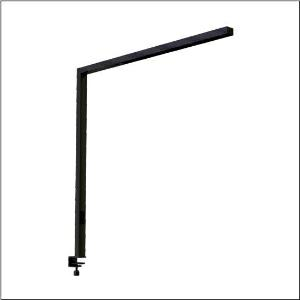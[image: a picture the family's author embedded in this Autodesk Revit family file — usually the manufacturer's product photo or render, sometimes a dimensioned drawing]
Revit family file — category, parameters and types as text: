
# Revit family: silica_r__31_desk_51my52gatcb_ad62
name_source: partatom
category: Lighting Fixtures
units: mm (PartAtom-declared; Revit-internal decimal feet)

## family parameters
Cut with Voids When Loaded = No
Host = Face
Light Source = No
Part Type = Normal
Room Calculation Point = No
Round Connector Dimension = Use Diameter
Shared = No

## types (1)
- --- (1 x LED, 8520 lm, 71 W, 4000K)
    Apparent Load = 71 VA
    CIE Flux Codes = 86 100 100 24 100
    Color Rendering = 80
    Color Temperature = 4000K
    Default Elevation = 1800 mm
    Description = Silica® 31 Desk, desktop luminaire, secondary optical cover: cover panel, of PMMA, light emission: direct/indirect distribution, primary light characteristic: symmetric, installation type: as desk luminaire, LED, rated luminous flux: 8.520lm, luminous efficacy: 120lm/W, light colour: 8tw, colour temperature: 2700..6500K, daylight-dependent control, with cable with plug, mains connection: 230V, AC, 50Hz, connection cable pre-assembled, rated input power: 71W, luminaire head, of aluminium, jet black (RAL 9005), length: 1.203mm, width: 52mm, supporting column, angular, of aluminium, jet black (RAL 9005), baseplate, of steel, jet black (RAL 9005), protection rating (complete): IP20, insulation class (complete): insulation class I (protective earthing), certification: CE, permissible operating ambient temperature: -20..+40°C, standard: EN 50419, packaging unit: 1 piece
    Height = 36 mm
    Lamp = 1 x LED
    Lamp Light Flux = 8520 lm
    Lamp Power = 71 W
    Lamp count = 1
    Length = 1203 mm
    Luminous efficacy = 120 lm/W
    Manufacturer = Siteco
    ModVariant = No
    Model = 51MY52GATCB
    Mounting Place = Floor
    Mounting Type = Freestanding
    Number of Poles = 1
    OnlyDefault = Yes
    Power Factor = 1
    Product Name = Silica® 31 Desk
    Product group = desktop luminaire
    ProductGroupID = 1302
    Protection Class = Protection class I
    Protection Degree = IP 20
    RLX_Detail_Level = 1
    RLX_Emergency_Light_Flux = 0 lm
    RLX_Emergency_Type = 0
    RLX_Emergency_Type_DB = No
    RlxData = <blob elided: 19101 chars, md5=9f7b484b>
    Socket = socket
    Standby Power = 0 W
    System Light Flux = 8520 lm
    System Power = 71 W
    Type Comments = factory setting
    Type Image = l_1275329.jpg
    URL = http://relux.com
    VarID = @adj_032445
    Voltage = 0 V
    Weight = 0.00 kg
    Width = 52 mm  [stored 0.170604 ft]

note: [stored X ft] marks values corroborated as IEEE doubles in the binary element streams (Revit-internal decimal feet)

## geometry (parser evidence)
native form markers: Blend x4, Sweep x16
no freeform markers — native parametric forms only
